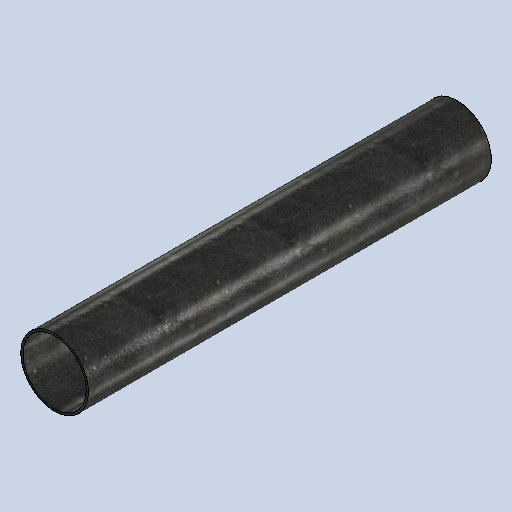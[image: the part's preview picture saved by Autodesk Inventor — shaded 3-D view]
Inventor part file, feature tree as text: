
AUTODESK INVENTOR PART (.ipt)
format: ipt  version: 2025.1 (Build 291241020, 241B)  size: 183,296 bytes
history: native  units: mm
features: extrude x1, sketch x1
ambient origin geometry x8: Origin, YZ Plane, XZ Plane, XY Plane, X Axis, Y Axis, Z Axis, Center Point
bodies: Solid1 (feature_tree)
feature tree (2):
  extrude  "Extrusion1"  Depth=535.0mm
  sketch  "Sketch1"  dims[d0=90.0mm d1=3.0mm d2=535.0mm d3=0.0mm]
